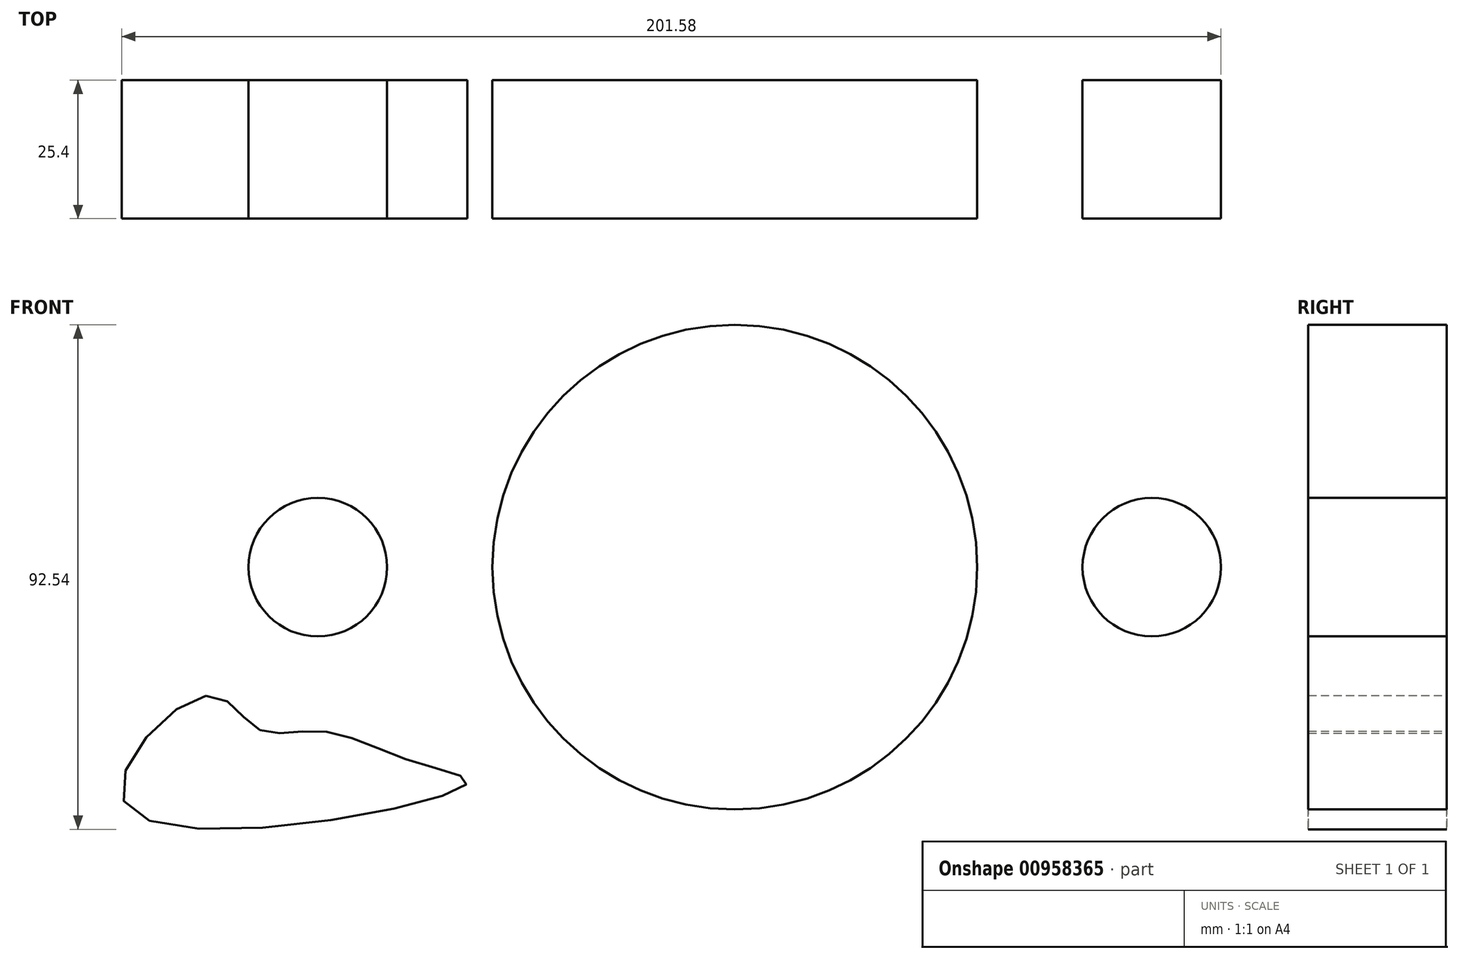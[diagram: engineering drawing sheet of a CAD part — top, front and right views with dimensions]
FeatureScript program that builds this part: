
annotation { "Feature Type Name" : "Feature", "Feature Type Description" : "" }
export const myFeature = defineFeature(function(context is Context, id is Id, definition is map)
    precondition{}
    {
        {
            var Q0;
            Q0=qCreatedBy(makeId("Front.planeOp"),FACE);
            var sketch = newSketch(context, id + "F0", { "sketchPlane" : qUnion([Q0])});
            skCircle(sketch, "E0", {"center": v(0, 0) * mm, "radius": 44.45 * mm});
            skArc(sketch, "E1", {"start": v(-46.43, -43.31) * mm, "mid": v(0, -63.5) * mm, "end": v(46.43, -43.31) * mm});
            skCircle(sketch, "E2", {"center": v(-76.46, 0) * mm, "radius": 12.7 * mm});
            skCircle(sketch, "E3.MirrorC", {"center": v(76.46, 0) * mm, "radius": 12.7 * mm});
            skArc(sketch, "E4", {"start": v(-97.7, 22.76) * mm, "mid": v(-110.83, -0.62) * mm, "end": v(-97, -23.6) * mm});
            skArc(sketch, "E5.MirrorCS", {"start": v(97.7, 22.76) * mm, "mid": v(110.83, -0.62) * mm, "end": v(97, -23.6) * mm});
            skFitSpline(sketch, "E6", {"points": [v(-97, -23.6) * mm, v(-87.6, -29.6) * mm, v(-76.07, -30.1) * mm, v(-57.97, -35.99) * mm, v(-49.35, -39.96) * mm, v(-111.36, -44.02) * mm, v(-97, -23.6) * mm]});
            skPoint(sketch, "E7.start.orphan", {"position": v(-87.6, -30.52) * mm});
            skFitSpline(sketch, "E8", {"points": [v(-97.7, 22.76) * mm, v(-77.87, 25.8) * mm, v(-64.22, 32.89) * mm, v(-46.43, 43.31) * mm, v(-46.43, 43.31) * mm, v(-50.82, -38.07) * mm, v(-50.82, -38.07) * mm, v(-76.07, -30.1) * mm, v(-97.18, -23.62) * mm, v(-97.7, 22.76) * mm]});
            skFitSpline(sketch, "E9.MirrorCS", {"points": [v(-97.7, -22.76) * mm, v(-77.87, -25.8) * mm, v(-64.22, -32.89) * mm, v(-46.43, -43.31) * mm, v(-46.43, -43.31) * mm, v(-50.82, 38.07) * mm, v(-50.82, 38.07) * mm, v(-76.07, 30.1) * mm, v(-97.18, 23.62) * mm, v(-97.7, -22.76) * mm]});
            skFitSpline(sketch, "E10.MirrorCS", {"points": [v(97.7, 22.76) * mm, v(77.87, 25.8) * mm, v(64.22, 32.89) * mm, v(46.43, 43.31) * mm, v(46.43, 43.31) * mm, v(50.82, -38.07) * mm, v(50.82, -38.07) * mm, v(76.07, -30.1) * mm, v(97.18, -23.62) * mm, v(97.7, 22.76) * mm]});
            skFitSpline(sketch, "E11.MirrorCS", {"points": [v(97.7, -22.76) * mm, v(77.87, -25.8) * mm, v(64.22, -32.89) * mm, v(46.43, -43.31) * mm, v(46.43, -43.31) * mm, v(50.82, 38.07) * mm, v(50.82, 38.07) * mm, v(76.07, 30.1) * mm, v(97.18, 23.62) * mm, v(97.7, -22.76) * mm]});
            skArc(sketch, "E12.trimOffspring", {"start": v(46.43, 43.31) * mm, "mid": v(0, 63.5) * mm, "end": v(-46.43, 43.31) * mm});
            skSolve(sketch);
        }
        {
            var Q0;
            Q0 = qSketchRegion(id + "F0", true);
            extrude(context, id + "F1", {"entities" : qUnion([Q0]), "depth" : 25.4 * mm, "offsetDistance" : 25.4 * mm});
        }
    });
